# Revit family: MPFR-DW
name_source: partatom
category: Generic Models
units: mm (PartAtom-declared; Revit-internal decimal feet)

## family parameters
Can host rebar = No
Cut with Voids When Loaded = No
Host = Face
Maintain Annotation Orientation = No
Part Type = Normal
Room Calculation Point = No
Round Connector Dimension = Use Diameter
Shared = No

## types (18) — shared parameters
Default Elevation = 4' - 0"
Description = INSULATED FIRE RATED ACCESS DOOR W/ DRYWALL BEAD FRAME
Manufacturer = MIFAB
Material = <By Category>
Model = MPFR-DW
URL = WWW.MIFAB.COM

## per-type parameters (varying)
| type | Height | Width |
| MFRU-12” x 12” | 1' - 0" | 1' - 0" |
| MFRU-8” x 8” | 0' - 8" | 0' - 8" |
| MFRU-10” x 10” | 0' - 10" | 0' - 10" |
| MFRU-12” x 18” | 1' - 6" | 1' - 0" |
| MFRU-12” x 24” | 2' - 0" | 1' - 0" |
| MFRU-14” x 14” | 1' - 2" | 1' - 2" |
| MFRU-16” x 16” | 1' - 4" | 1' - 4" |
| MFRU-18” x 18” | 1' - 6" | 1' - 6" |
| MFRU-20” x 20” | 1' - 8" | 1' - 8" |
| MFRU-22” x 22” | 1' - 10" | 1' - 10" |
| MFRU-22” x 30” | 2' - 6" | 1' - 10" |
| MFRU-24” x 24” | 2' - 0" | 2' - 0" |
| MFRU-24” x 36” | 3' - 0" | 2' - 0" |
| MFRU-24” x 48” | 4' - 0" | 2' - 0" |
| MFRU-30” x 30” | 2' - 6" | 2' - 6" |
| MFRU-32” x 32” | 2' - 8" | 2' - 8" |
| MFRU-36” x 36” | 3' - 0" | 3' - 0" |
| MFRU-36” x 48” | 4' - 0" | 3' - 0" |

## geometry (parser evidence)
native form markers: Sweep x8
no freeform markers — native parametric forms only
